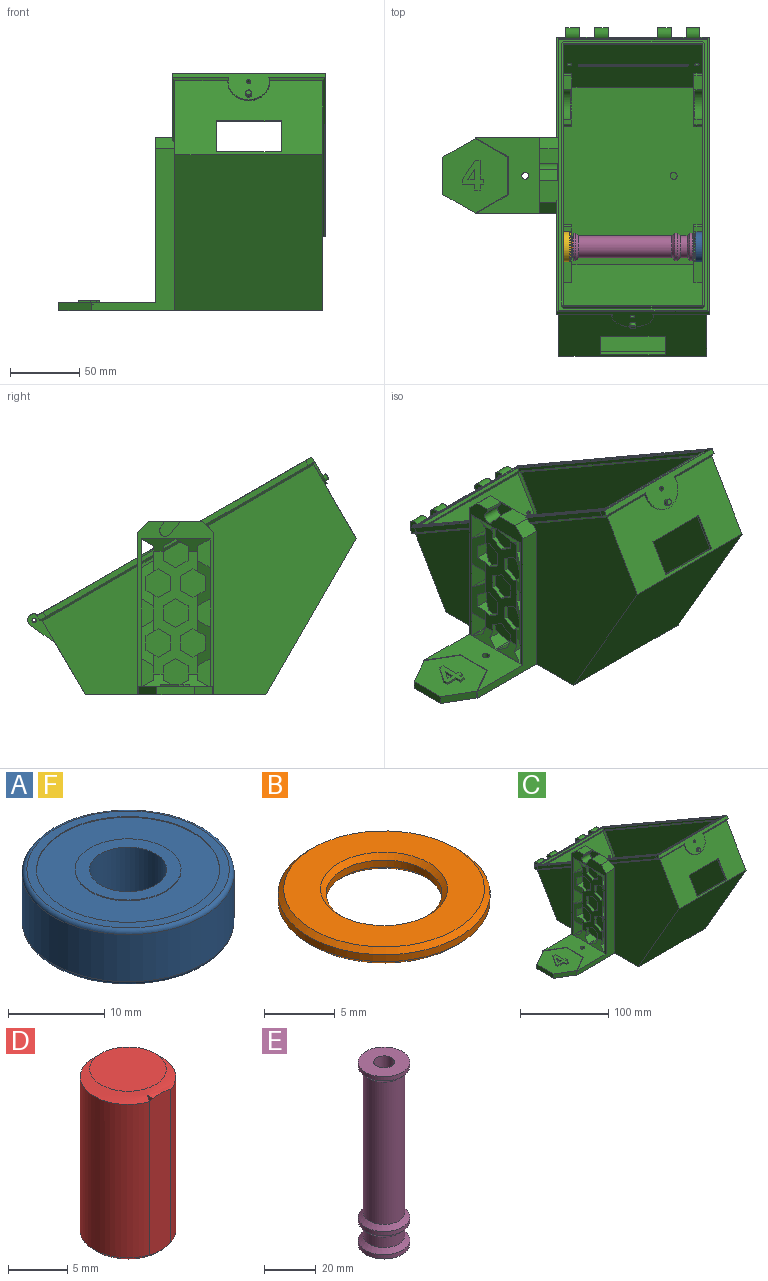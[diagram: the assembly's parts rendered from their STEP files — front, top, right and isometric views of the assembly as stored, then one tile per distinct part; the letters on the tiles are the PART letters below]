
ASSEMBLY  parts=6 mates=5
PART A: 14 faces, bbox 23.8x23.8x7 mm
  f0: cylinder r=5.5mm len=11mm, axis (0,0,-1), area 3.5mm2, adj f4,f6
  f1: cylinder r=4mm len=8mm, axis (0,0,-1), area 175.9mm2, adj f3,f4
  f2: cylinder r=5.5mm len=11mm, axis (0,0,-1), area 3.5mm2, adj f3,f5
  f3: plane 11x11mm, normal (0,0,1), area 44.8mm2, adj f1,f2
  f4: plane 11x11mm, normal (0,0,-1), area 44.8mm2, adj f0,f1
  f5: plane 19x19mm, normal (0,0,1), area 188.5mm2, adj f2,f8
  f6: plane 19x19mm, normal (0,0,-1), area 188.5mm2, adj f0,f7
  f7: cylinder r=9.5mm len=19mm, axis (0,0,-1), area 6mm2, adj f6,f11
  f8: cylinder r=9.5mm len=19mm, axis (0,0,-1), area 6mm2, adj f5,f10
  f9: cylinder r=11mm len=22mm, axis (0,0,-1), area 414.7mm2, adj f12,f13
  f10: plane 21x21mm, normal (0,0,1), area 62.8mm2, adj f8,f13
  f11: plane 21x21mm, normal (0,0,-1), area 62.8mm2, adj f7,f12
  f12: torus R=10.5mm, axis (0,0,1), area 53.4mm2, adj f9,f11
  f13: torus R=10.5mm, axis (0,0,1), area 53.4mm2, adj f9,f10
PART B: 8 faces, bbox 15x15x1.4 mm
  f0: cylinder r=4.1mm len=8.2mm, axis (0,0,-1), area 15.5mm2, adj f5,f7
  f1: cylinder r=7.5mm len=15mm, axis (0,0,-1), area 28.3mm2, adj f4,f6
  f2: plane 14.2x14.2mm, normal (0,0,1), area 94.8mm2, adj f4,f5
  f3: plane 14.2x14.2mm, normal (0,0,-1), area 94.8mm2, adj f6,f7
  f4: cone r=7.1mm half-angle=45deg, axis (0,0,-1), area 25.9mm2, adj f1,f2
  f5: cone r=4.1mm half-angle=45deg, axis (0,0,1), area 15.3mm2, adj f0,f2
  f6: cone r=7.5mm half-angle=45deg, axis (0,0,1), area 25.9mm2, adj f1,f3
  f7: cone r=4.5mm half-angle=45deg, axis (0,0,-1), area 15.3mm2, adj f0,f3
PART C: 307 faces, bbox 193.2x238.3x172.8 mm
  f0: cylinder r=2.5mm len=5mm, axis (0,0,-1), area 22mm2, adj f1,f55
  f1: plane 5x5mm, normal (0,0,1), area 19.6mm2, adj f0
  f2: cylinder r=1.6mm len=10mm, axis (-1,0,0), area 100.5mm2, adj f244,f253
  f3: cylinder r=1.6mm len=10mm, axis (-1,0,0), area 100.5mm2, adj f238,f240
  f4: plane 107.8x0.92mm, normal (0,1,-0.01), area 98.9mm2, adj f5,f26,f302,f303
  f5: plane 107.8x1.04mm, normal (0,0.87,-0.5), area 129.4mm2, adj f4,f302,f303,f306
  f6: plane 107.8x0.79mm, normal (0,-0.51,0.86), area 98.9mm2, adj f7,f26,f301,f302
  f7: plane 107.8x1.04mm, normal (0,-0.87,0.5), area 129.4mm2, adj f6,f301,f302,f306
  f8: plane 198.81x115.33mm, normal (-0.71,-0.35,-0.61), area 432.4mm2, adj f9,f10,f11,f12,f13,f251,f252,f257
  f9: plane 227.12x166.81mm, normal (-1,0,0), area 21083.7mm2, adj f8,f13,f227,f228,f229,f230,f285,f289
  f10: plane 70.94x40.96mm, normal (0,-0.5,-0.87), area 8.9mm2, adj f8,f13,f252,f253,f254,f255,f256,f284
  f11: plane 26.85x15.5mm, normal (0,-0.5,-0.87), area 3.1mm2, adj f8,f257,f282,f299
  f12: plane 78.58x45.37mm, normal (0,-0.5,-0.87), area 13.2mm2, adj f8,f247,f248,f249,f250,f251,f290,f305
  f13: plane 117.98x60.6mm, normal (0,1,0), area 1916.5mm2, adj f8,f9,f10,f26,f30,f283,f284,f285
  f14: cone r=2.1mm half-angle=45deg, axis (0,0.87,-0.5), area 5.6mm2, adj f15,f16
  f15: cylinder r=2.25mm len=5.25mm, axis (0,-0.87,0.5), area 38.2mm2, adj f14,f249
  f16: plane 3.9x3.38mm, normal (0,-0.87,0.5), area 11.9mm2, adj f14
  f17: plane 2.48x2.3mm, normal (-0.71,0.61,-0.35), area 4.2mm2, adj f18,f19,f25,f306
  f18: plane 100.55x1.73mm, normal (0,0.87,-0.5), area 201.1mm2, adj f17,f19,f20,f306
  f19: plane 192.23x110.99mm, normal (0,0.5,0.87), area 835.1mm2, adj f17,f18,f20,f21,f22,f23,f24,f25
  f20: plane 2.48x2.3mm, normal (0.71,0.61,-0.35), area 4.2mm2, adj f18,f19,f21,f306
  f21: plane 190.63x111.22mm, normal (1,0,0), area 437.9mm2, adj f19,f20,f22,f306
  f22: plane 2.48x2.3mm, normal (0.71,-0.61,0.35), area 4.2mm2, adj f19,f21,f23,f306
  f23: plane 100.55x1.73mm, normal (0,-0.87,0.5), area 201.1mm2, adj f19,f22,f24,f306
  f24: plane 2.48x2.3mm, normal (-0.71,-0.61,0.35), area 4.2mm2, adj f19,f23,f25,f306
  f25: plane 190.63x111.22mm, normal (-1,0,0), area 437.9mm2, adj f17,f19,f24,f306
  f26: plane 198.99x114.89mm, normal (0,0.5,0.87), area 678.3mm2, adj f4,f6,f13,f27,f30,f231,f232,f233
  f27: plane 39x13.71mm, normal (0,0,1), area 373.2mm2, adj f26,f30,f290,f293,f294,f295,f296,f297
  f28: plane 0.7x0.68mm, normal (0.85,-0.52,0), area 0.2mm2, adj f29,f30,f276,f298
  f29: plane 0.47x0.29mm, normal (0,0.5,0.87), area 0.1mm2, adj f28,f30,f276
  f30: plane 193.23x112.72mm, normal (1,0,0), area 870.7mm2, adj f13,f26,f27,f28,f29,f281,f297,f298
  f31: plane 7.34x4.94mm, normal (0,0,1), area 18.1mm2, adj f50,f51,f52
  f32: plane 17.29x7.95mm, normal (0,0,1), area 120.8mm2, adj f41,f42,f46,f53,f54,f72,f76
  f33: plane 17.29x7.95mm, normal (0,0,1), area 120.8mm2, adj f35,f36,f48,f56,f57,f73,f76
  f34: plane 22.1x13.04mm, normal (1,0,0), area 73.5mm2, adj f49,f59,f60,f61
  f35: plane 22.1x13.04mm, normal (1,0,0), area 73.5mm2, adj f33,f36,f48,f61
  f36: cylinder r=8.98mm len=17.96mm, axis (-1,0,0), area 24.2mm2, adj f33,f35,f56,f61
  f37: plane 7.85x1.5mm, normal (0,0.71,0.71), area 15.1mm2, adj f39,f40,f56,f61
  f38: plane 21.53x6.35mm, normal (0,1,0), area 136.7mm2, adj f43,f54,f55,f63
  f39: plane 21.53x6.35mm, normal (0,1,0), area 136.7mm2, adj f37,f55,f56,f65
  f40: plane 74.11x1.5mm, normal (-0.71,0,0.71), area 154mm2, adj f37,f61,f62,f65
  f41: cylinder r=8.98mm len=17.96mm, axis (-1,0,0), area 24.2mm2, adj f32,f42,f54,f66
  f42: plane 22.1x13.04mm, normal (-1,0,0), area 73.5mm2, adj f32,f41,f46,f66
  f43: plane 7.85x1.5mm, normal (0,0.71,0.71), area 15.1mm2, adj f38,f45,f54,f66
  f44: plane 22.1x13.04mm, normal (-1,0,0), area 73.5mm2, adj f47,f66,f67,f68
  f45: plane 74.11x1.5mm, normal (0.71,0,0.71), area 154mm2, adj f43,f63,f66,f70
  f46: cylinder r=11.05mm len=22.1mm, axis (-1,0,0), area 278.8mm2, adj f32,f42,f66,f72
  f47: cylinder r=11.05mm len=22.1mm, axis (1,0,0), area 278.8mm2, adj f44,f66,f68,f72
  f48: cylinder r=11.05mm len=22.1mm, axis (-1,0,0), area 278.8mm2, adj f33,f35,f61,f73
  f49: cylinder r=11.05mm len=22.1mm, axis (1,0,0), area 278.8mm2, adj f34,f59,f61,f73
  f50: plane 7.34x1.5mm, normal (-1,0,0), area 11mm2, adj f31,f51,f52,f74
  f51: plane 7.34x4.94mm, normal (0.83,-0.56,0), area 13.3mm2, adj f31,f50,f52,f74
  f52: plane 4.94x1.5mm, normal (0,1,0), area 7.4mm2, adj f31,f50,f51,f74
  f53: plane 88.26x52mm, normal (0.71,0.61,0.35), area 228.8mm2, adj f32,f72,f75,f76
  f54: plane 41.99x23.03mm, normal (1,0,0), area 650.7mm2, adj f32,f38,f41,f43,f55,f66,f76
  f55: plane 128.5x100.95mm, normal (0,0,1), area 12223.7mm2, adj f0,f38,f39,f54,f56,f63,f64,f65
  f56: plane 41.99x23.03mm, normal (-1,0,0), area 650.7mm2, adj f33,f36,f37,f39,f55,f61,f76
  f57: plane 88.26x52mm, normal (-0.71,0.61,0.35), area 228.8mm2, adj f33,f73,f76,f77
  f58: plane 6.35x3.4mm, normal (0,0.87,-0.5), area 24.9mm2, adj f59,f78,f79,f80
  f59: plane 17.29x7.95mm, normal (0,0,1), area 87.8mm2, adj f34,f49,f58,f60,f73,f78,f80,f91
  f60: cylinder r=8.98mm len=17.96mm, axis (1,0,0), area 24.2mm2, adj f34,f59,f61,f80
  f61: plane 85.49x7.95mm, normal (0,0,1), area 67.4mm2, adj f34,f35,f36,f37,f40,f48,f49,f56
  f62: plane 7.85x1.5mm, normal (0,-0.71,0.71), area 15.1mm2, adj f40,f61,f64,f80
  f63: plane 71.11x21.53mm, normal (1,0,0), area 1530.8mm2, adj f38,f45,f55,f69
  f64: plane 21.53x6.35mm, normal (0,-1,0), area 136.7mm2, adj f55,f62,f65,f80
  f65: plane 71.11x21.53mm, normal (-1,0,0), area 1530.8mm2, adj f39,f40,f55,f64
  f66: plane 85.49x7.95mm, normal (0,0,1), area 67.4mm2, adj f41,f42,f43,f44,f45,f46,f47,f54
  f67: cylinder r=8.98mm len=17.96mm, axis (1,0,0), area 24.2mm2, adj f44,f66,f68,f81
  f68: plane 17.29x7.95mm, normal (0,0,1), area 87.8mm2, adj f44,f47,f67,f71,f72,f81,f83,f86
  f69: plane 21.53x6.35mm, normal (0,-1,0), area 136.7mm2, adj f55,f63,f70,f81
  f70: plane 7.85x1.5mm, normal (0,-0.71,0.71), area 15.1mm2, adj f45,f66,f69,f81
  f71: plane 6.35x3.4mm, normal (0,0.87,-0.5), area 24.9mm2, adj f68,f81,f82,f83
  f72: plane 220.59x154.32mm, normal (1,0,0), area 17869.6mm2, adj f32,f46,f47,f53,f66,f68,f85,f86
  f73: plane 220.59x154.32mm, normal (-1,0,0), area 17869.6mm2, adj f33,f48,f49,f57,f59,f61,f89,f90
  f74: plane 21.56x15.44mm, normal (0,0,1), area 165.5mm2, adj f50,f51,f52,f92,f93,f94,f95,f96
  f75: plane 2.77x1.6mm, normal (0.55,0.84,0), area 2.6mm2, adj f53,f87,f103
  f76: plane 109.9x100.95mm, normal (0,0.87,0.5), area 12473mm2, adj f32,f33,f53,f54,f55,f56,f57,f103
  f77: plane 2.77x1.6mm, normal (-0.55,0.84,0), area 2.6mm2, adj f57,f89,f103
  f78: plane 7.16x5.65mm, normal (-1,0,0), area 23.5mm2, adj f58,f59,f79,f108
  f79: plane 6.35x3.9mm, normal (0,0.5,0.87), area 28.6mm2, adj f58,f78,f80,f108
  f80: plane 38.73x23.03mm, normal (-1,0,0), area 627.2mm2, adj f55,f58,f59,f60,f61,f62,f64,f79
  f81: plane 38.73x23.03mm, normal (1,0,0), area 627.2mm2, adj f55,f66,f67,f68,f69,f70,f71,f82
  f82: plane 6.35x3.9mm, normal (0,0.5,0.87), area 28.6mm2, adj f71,f81,f83,f108
  f83: plane 7.16x5.65mm, normal (1,0,0), area 23.5mm2, adj f68,f71,f82,f108
  f84: plane 101.15x0.09mm, normal (0,-0.5,-0.87), area 10.1mm2, adj f86,f91,f108,f111
  f85: plane 190.15x109.79mm, normal (0,-0.5,-0.87), area 21.9mm2, adj f72,f86,f87,f112
  f86: plane 31.8x19.63mm, normal (0.71,-0.61,0.35), area 82.2mm2, adj f68,f72,f84,f85,f108,f111,f112
  f87: plane 54.03x31.66mm, normal (0.71,0.61,-0.35), area 138.5mm2, adj f72,f75,f85,f88,f110,f112,f113
  f88: plane 101.15x0.09mm, normal (0,-0.5,-0.87), area 10.1mm2, adj f87,f89,f110,f113
  f89: plane 54.03x31.66mm, normal (-0.71,0.61,-0.35), area 138.5mm2, adj f73,f77,f88,f90,f110,f113,f114
  f90: plane 190.15x109.79mm, normal (0,-0.5,-0.87), area 21.9mm2, adj f73,f89,f91,f114
  f91: plane 31.8x19.63mm, normal (-0.71,-0.61,0.35), area 82.2mm2, adj f59,f73,f84,f90,f108,f111,f114
  f92: plane 3.98x1.5mm, normal (0,-1,0), area 6mm2, adj f74,f93,f102,f116
  f93: plane 4.32x1.5mm, normal (1,0,0), area 6.5mm2, adj f74,f92,f94,f116
  f94: plane 2.67x1.5mm, normal (0,-1,0), area 4mm2, adj f74,f93,f95,f116
  f95: plane 3.62x1.5mm, normal (1,0,0), area 5.4mm2, adj f74,f94,f96,f116
  f96: plane 2.67x1.5mm, normal (0,1,0), area 4mm2, adj f74,f95,f97,f116
  f97: plane 13.62x1.5mm, normal (1,0,0), area 20.4mm2, adj f74,f96,f98,f116
  f98: plane 3.46x1.5mm, normal (0,1,0), area 5.2mm2, adj f74,f97,f99,f116
  f99: plane 13.64x9.32mm, normal (-0.83,0.56,0), area 24.8mm2, adj f74,f98,f100,f116
  f100: plane 3.6x1.5mm, normal (-1,0,0), area 5.4mm2, adj f74,f99,f101,f116
  f101: plane 8.79x1.5mm, normal (0,-1,0), area 13.2mm2, adj f74,f100,f102,f116
  f102: plane 4.32x1.5mm, normal (-1,0,0), area 6.5mm2, adj f74,f92,f101,f116
  f103: plane 100.95x2.77mm, normal (0,1,0), area 249.2mm2, adj f75,f76,f77,f110,f117,f118,f119
  f104: cylinder r=1.75mm len=3.5mm, axis (0,1,0), area 5.6mm2, adj f105,f107,f108,f122
  f105: plane 76.2x1.11mm, normal (0,0,-1), area 84.5mm2, adj f104,f106,f108,f123
  f106: cylinder r=1.75mm len=3.5mm, axis (0,1,0), area 5.6mm2, adj f105,f107,f108,f124
  f107: plane 76.2x1.11mm, normal (0,0,1), area 84.5mm2, adj f104,f106,f108,f125
  f108: plane 101.37x54.25mm, normal (0,-0.87,0.5), area 5684.1mm2, adj f55,f78,f79,f80,f81,f82,f83,f84
  f109: plane 198.81x115.33mm, normal (0.71,-0.35,-0.61), area 483.8mm2, adj f121,f126,f136,f141
  f110: plane 100.95x52.44mm, normal (0,0.87,-0.5), area 4902.8mm2, adj f87,f88,f89,f103,f117,f119,f120,f147
  f111: plane 102.55x2.05mm, normal (0,-0.97,-0.26), area 215.9mm2, adj f84,f86,f91,f112,f114,f163
  f112: plane 191.37x111.03mm, normal (0.71,-0.35,-0.61), area 467.2mm2, adj f85,f86,f87,f111,f113,f164
  f113: plane 102.55x2.05mm, normal (0,0.26,-0.97), area 215.9mm2, adj f87,f88,f89,f112,f114,f165
  f114: plane 191.37x111.03mm, normal (-0.71,-0.35,-0.61), area 467.2mm2, adj f89,f90,f91,f111,f113,f166
  f115: plane 22.98x9mm, normal (-0.85,0,0.52), area 117mm2, adj f181,f183,f207,f216,f217,f218
  f116: plane 54.04x46.81mm, normal (0,0,1), area 1713.2mm2, adj f92,f93,f94,f95,f96,f97,f98,f99
  f117: plane 23.94x14.88mm, normal (1,0,0), area 52.7mm2, adj f103,f110,f118,f120,f227
  f118: plane 46.7x2.02mm, normal (0,0.5,0.87), area 108.7mm2, adj f103,f117,f119,f227
  f119: plane 23.94x14.88mm, normal (-1,0,0), area 52.7mm2, adj f103,f110,f118,f120,f227
  f120: plane 46.7x1.73mm, normal (0,-0.5,-0.87), area 93.4mm2, adj f110,f117,f119,f227
  f121: plane 40.6x2.06mm, normal (0,-0.97,-0.26), area 84.2mm2, adj f109,f141,f142,f227
  f122: bspline ~5.58x3.82mm, area 13mm2, adj f104,f123,f125,f230
  f123: plane 76.2x1.8mm, normal (0,0.5,-0.87), area 158.4mm2, adj f105,f122,f124,f230
  f124: bspline ~5.58x3.82mm, area 13mm2, adj f106,f123,f125,f230
  f125: plane 76.2x1.04mm, normal (0,0.87,0.5), area 91.4mm2, adj f107,f122,f124,f230
  f126: plane 227.12x166.81mm, normal (1,0,0), area 21412.8mm2, adj f109,f227,f228,f229,f230
  f127: cylinder r=1.6mm len=3.77mm, axis (0,-0.87,0.5), area 20.1mm2, adj f108,f230
  f128: cylinder r=1.6mm len=3.77mm, axis (0,-0.87,0.5), area 20.1mm2, adj f108,f230
  f129: plane 35.59x0.09mm, normal (0,-0.5,-0.87), area 3.6mm2, adj f130,f232,f233,f234
  f130: plane 35.59x2.05mm, normal (0,0.26,-0.97), area 75.5mm2, adj f129,f230,f232,f234
  f131: cylinder r=1.35mm len=10mm, axis (-1,0,0), area 84.8mm2, adj f234,f236
  f132: plane 18.02x12.76mm, normal (0,0.58,-0.82), area 220.8mm2, adj f230,f234,f235,f236
  f133: plane 10.8x0.09mm, normal (0,-0.5,-0.87), area 1.1mm2, adj f134,f236,f237,f238
  f134: plane 10.8x2.05mm, normal (0,0.26,-0.97), area 22.9mm2, adj f133,f230,f236,f238
  f135: plane 18.02x12.76mm, normal (0,0.58,-0.82), area 220.8mm2, adj f230,f238,f239,f240
  f136: plane 6.5x2.05mm, normal (0,0.26,-0.97), area 12.2mm2, adj f109,f141,f230,f240
  f137: cylinder r=1.35mm len=10mm, axis (-1,0,0), area 84.8mm2, adj f232,f246
  f138: plane 18.02x12.76mm, normal (0,0.58,-0.82), area 220.8mm2, adj f230,f231,f232,f246
  f139: plane 10.8x0.09mm, normal (0,-0.5,-0.87), area 1.1mm2, adj f140,f244,f245,f246
  f140: plane 10.8x2.05mm, normal (0,0.26,-0.97), area 22.9mm2, adj f139,f230,f244,f246
  f141: plane 198.99x114.89mm, normal (0,-0.5,-0.87), area 27.7mm2, adj f109,f121,f136,f142,f240,f241,f242,f249
  f142: cylinder r=15.01mm len=9.72mm, axis (0,-0.87,0.5), area 15.8mm2, adj f121,f141,f143,f227,f249
  f143: plane 1.92x1.72mm, normal (0.86,-0.25,-0.44), area 2mm2, adj f142,f144,f227,f249
  f144: cylinder r=15.01mm len=12.11mm, axis (0,-0.87,0.5), area 23.2mm2, adj f143,f145,f227,f249
  f145: plane 1.39x1.23mm, normal (-0.01,-0.5,-0.87), area 2mm2, adj f144,f146,f227,f249
  f146: cylinder r=15.01mm len=12.03mm, axis (0,-0.87,0.5), area 23.2mm2, adj f145,f148,f227,f249
  f147: cylinder r=1.6mm len=4.72mm, axis (0,0.87,-0.5), area 36.2mm2, adj f110,f249
  f148: plane 1.92x1.73mm, normal (-0.87,-0.25,-0.43), area 2mm2, adj f146,f227,f249,f250
  f149: plane 18.02x12.76mm, normal (0,0.58,-0.82), area 220.8mm2, adj f230,f243,f244,f253
  f150: plane 14x9mm, normal (0,-0.5,-0.87), area 88.3mm2, adj f151,f260,f265,f267
  f151: plane 10.39x8.36mm, normal (0,-1,0), area 42.9mm2, adj f150,f152,f187,f214,f260,f267
  f152: plane 22.98x9mm, normal (-0.85,0,0.52), area 117mm2, adj f151,f186,f207,f212,f213,f214,f267
  f153: plane 10.39x9.72mm, normal (0,1,0), area 101mm2, adj f188,f192,f260,f267
  f154: plane 10.39x9.72mm, normal (0,1,0), area 101mm2, adj f193,f197,f260,f267
  f155: plane 14x9mm, normal (0,-0.5,-0.87), area 88.3mm2, adj f156,f260,f266,f267
  f156: plane 10.39x3mm, normal (0,-1,0), area 31.2mm2, adj f155,f157,f260,f267
  f157: plane 14x9mm, normal (0,-0.5,0.87), area 88.3mm2, adj f156,f260,f266,f267
  f158: plane 14x9mm, normal (0,-0.5,0.87), area 88.3mm2, adj f160,f260,f267,f268
  f159: plane 14x9mm, normal (0,-0.5,-0.87), area 108.9mm2, adj f160,f258,f259,f268,f269,f270
  f160: plane 10.39x7.29mm, normal (0,-1,0), area 38.7mm2, adj f158,f159,f258,f260,f267,f270
  f161: plane 10.39x9.72mm, normal (0,-1,0), area 101mm2, adj f167,f171,f210,f272
  f162: plane 10.39x9.72mm, normal (0,-1,0), area 101mm2, adj f175,f179,f209,f274
  f163: plane 100.95x2.17mm, normal (0,-0.87,0.5), area 252.4mm2, adj f19,f111,f164,f166
  f164: plane 191.23x111.85mm, normal (1,0,0), area 548.4mm2, adj f19,f112,f163,f165
  f165: plane 100.95x2.17mm, normal (0,0.87,-0.5), area 252.4mm2, adj f19,f113,f164,f166
  f166: plane 191.23x111.85mm, normal (-1,0,0), area 548.4mm2, adj f19,f114,f163,f165
  f167: plane 9.72x9mm, normal (0,-0.5,-0.87), area 52.5mm2, adj f161,f168,f207,f210,f272,f278
  f168: plane 9x5.2mm, normal (0,0.5,-0.87), area 31.2mm2, adj f167,f169,f207,f278
  f169: plane 10.39x3mm, normal (0,1,0), area 31.2mm2, adj f168,f170,f207,f278
  f170: plane 9x5.2mm, normal (0,0.5,0.87), area 31.2mm2, adj f169,f171,f207,f278
  f171: plane 9.72x9mm, normal (0,-0.5,0.87), area 52.5mm2, adj f161,f170,f207,f210,f272,f278
  f172: plane 14x9mm, normal (0,0.5,-0.87), area 88.3mm2, adj f173,f207,f210,f272,f273,f278
  f173: plane 10.39x3mm, normal (0,1,0), area 31.2mm2, adj f172,f174,f207,f278
  f174: plane 14x9mm, normal (0,0.5,0.87), area 88.3mm2, adj f173,f207,f209,f273,f274,f278
  f175: plane 9.72x9mm, normal (0,-0.5,-0.87), area 52.5mm2, adj f162,f176,f207,f209,f274,f278
  f176: plane 9x5.2mm, normal (0,0.5,-0.87), area 31.2mm2, adj f175,f177,f207,f278
  f177: plane 10.39x3mm, normal (0,1,0), area 31.2mm2, adj f176,f178,f207,f278
  f178: plane 9x5.2mm, normal (0,0.5,0.87), area 31.2mm2, adj f177,f179,f207,f278
  f179: plane 9.72x9mm, normal (0,-0.5,0.87), area 52.5mm2, adj f162,f178,f207,f209,f274,f278
  f180: plane 14x9mm, normal (0,0.5,-0.87), area 88.3mm2, adj f181,f207,f209,f274,f275,f278
  f181: plane 10.39x8.36mm, normal (0,1,0), area 42.9mm2, adj f115,f180,f182,f207,f216,f278
  f182: plane 22.98x9mm, normal (0.85,0,0.52), area 117mm2, adj f181,f183,f215,f216,f218,f278
  f183: plane 10.39x8.36mm, normal (0,-1,0), area 42.9mm2, adj f115,f182,f184,f207,f218,f278
  f184: plane 9x5.2mm, normal (0,-0.5,-0.87), area 31.2mm2, adj f183,f185,f207,f278
  f185: plane 9x5.2mm, normal (0,0.5,-0.87), area 31.2mm2, adj f184,f186,f207,f278
  f186: plane 10.39x8.36mm, normal (0,1,0), area 42.9mm2, adj f152,f185,f187,f207,f212,f278
  f187: plane 22.98x9mm, normal (0.85,0,0.52), area 117mm2, adj f151,f186,f211,f212,f214,f260,f278
  f188: plane 9.72x9mm, normal (0,0.5,0.87), area 52.5mm2, adj f153,f189,f207,f260,f267,f278
  f189: plane 9x5.2mm, normal (0,-0.5,0.87), area 31.2mm2, adj f188,f190,f207,f278
  f190: plane 10.39x3mm, normal (0,-1,0), area 31.2mm2, adj f189,f191,f207,f278
  f191: plane 9x5.2mm, normal (0,-0.5,-0.87), area 31.2mm2, adj f190,f192,f207,f278
  f192: plane 9.72x9mm, normal (0,0.5,-0.87), area 52.5mm2, adj f153,f191,f207,f260,f267,f278
  f193: plane 9.72x9mm, normal (0,0.5,0.87), area 52.5mm2, adj f154,f194,f207,f260,f267,f278
  f194: plane 9x5.2mm, normal (0,-0.5,0.87), area 31.2mm2, adj f193,f195,f207,f278
  f195: plane 10.39x3mm, normal (0,-1,0), area 31.2mm2, adj f194,f196,f207,f278
  f196: plane 9x5.2mm, normal (0,-0.5,-0.87), area 31.2mm2, adj f195,f197,f207,f278
  f197: plane 9.72x9mm, normal (0,0.5,-0.87), area 52.5mm2, adj f154,f196,f207,f260,f267,f278
  f198: plane 10.39x7.29mm, normal (0,1,0), area 38.7mm2, adj f199,f207,f257,f258,f270,f278
  f199: plane 9x5.2mm, normal (0,0.5,0.87), area 31.2mm2, adj f198,f206,f207,f278
  f200: plane 9x5.2mm, normal (0,-0.5,0.87), area 31.2mm2, adj f201,f205,f207,f278
  f201: plane 10.39x3mm, normal (0,-1,0), area 31.2mm2, adj f200,f202,f207,f278
  f202: plane 9x5.2mm, normal (0,-0.5,-0.87), area 31.2mm2, adj f201,f203,f207,f278
  f203: plane 9x5.2mm, normal (0,0.5,-0.87), area 31.2mm2, adj f202,f204,f207,f278
  f204: plane 10.39x3mm, normal (0,1,0), area 31.2mm2, adj f203,f205,f207,f278
  f205: plane 9x5.2mm, normal (0,0.5,0.87), area 31.2mm2, adj f200,f204,f207,f278
  f206: plane 9x5.2mm, normal (0,-0.5,0.87), area 31.2mm2, adj f199,f207,f278,f279
  f207: plane 89.1x32mm, normal (-1,0,0), area 1421.1mm2, adj f115,f152,f167,f168,f169,f170,f171,f172
  f208: plane 14x9mm, normal (0,0.5,0.87), area 88.3mm2, adj f207,f210,f272,f277,f278,f299
  f209: plane 32.91x9mm, normal (0.85,-0.52,0), area 204.8mm2, adj f162,f174,f175,f179,f180,f278,f283
  f210: plane 32.91x9mm, normal (0.85,-0.52,0), area 204.8mm2, adj f161,f167,f171,f172,f208,f278,f283
  f211: plane 23.64x0.19mm, normal (1,0,0), area 4.4mm2, adj f187,f212,f214,f285
  f212: plane 14x8.32mm, normal (0,0.5,0.87), area 108.5mm2, adj f152,f186,f187,f211,f213,f285
  f213: plane 23.64x0.19mm, normal (-1,0,0), area 4.4mm2, adj f152,f212,f214,f285
  f214: plane 14x8.32mm, normal (0,-0.5,0.87), area 108.5mm2, adj f151,f152,f187,f211,f213,f285
  f215: plane 23.64x0.19mm, normal (1,0,0), area 4.4mm2, adj f182,f216,f218,f285
  f216: plane 14x8.32mm, normal (0,0.5,0.87), area 108.5mm2, adj f115,f181,f182,f215,f217,f285
  f217: plane 23.64x0.19mm, normal (-1,0,0), area 4.4mm2, adj f115,f216,f218,f285
  f218: plane 14x8.32mm, normal (0,-0.5,0.87), area 108.5mm2, adj f115,f182,f183,f215,f217,f285
  f219: plane 27.6x1.51mm, normal (-1,0,0), area 41.7mm2, adj f262,f285,f286,f287
  f220: plane 23.4x13.5mm, normal (0.5,-0.87,0), area 40.8mm2, adj f116,f221,f226,f287
  f221: plane 27.02x1.51mm, normal (1,0,0), area 40.8mm2, adj f116,f220,f222,f287
  f222: plane 23.4x13.52mm, normal (0.5,0.87,0), area 40.8mm2, adj f116,f221,f224,f287
  f223: cylinder r=2.5mm len=5.98mm, axis (0,0,-1), area 94mm2, adj f285,f289
  f224: plane 23.4x13.5mm, normal (-0.5,0.87,0), area 161.7mm2, adj f116,f222,f225,f288,f289
  f225: plane 27.02x5.98mm, normal (-1,0,0), area 161.7mm2, adj f116,f224,f226,f289
  f226: plane 23.4x13.52mm, normal (-0.5,-0.87,0), area 161.7mm2, adj f116,f220,f225,f261,f289
  f227: plane 107.19x53.53mm, normal (0,-0.87,0.5), area 4990.2mm2, adj f9,f117,f118,f119,f120,f121,f126,f142
  f228: plane 113.29x107.19mm, normal (0,-0.87,-0.5), area 14021.6mm2, adj f9,f126,f227,f229
  f229: plane 130.81x107.19mm, normal (0,0,-1), area 14021.6mm2, adj f9,f126,f228,f230
  f230: plane 107.19x53.53mm, normal (0,0.87,-0.5), area 5352.1mm2, adj f9,f122,f123,f124,f125,f126,f127,f128
  f231: cylinder r=4.65mm len=10mm, axis (-1,0,0), area 146.6mm2, adj f26,f138,f232,f246
  f232: plane 21.2x19.98mm, normal (1,0,0), area 132.6mm2, adj f26,f129,f130,f137,f138,f230,f231,f233
  f233: plane 35.59x3.46mm, normal (0,0.87,-0.5), area 142.4mm2, adj f26,f129,f232,f234
  f234: plane 21.2x19.98mm, normal (-1,0,0), area 132.6mm2, adj f26,f129,f130,f131,f132,f230,f233,f235
  f235: cylinder r=4.65mm len=10mm, axis (-1,0,0), area 146.6mm2, adj f26,f132,f234,f236
  f236: plane 21.2x19.98mm, normal (1,0,0), area 132.6mm2, adj f26,f131,f132,f133,f134,f230,f235,f237
  f237: plane 10.8x3.46mm, normal (0,0.87,-0.5), area 43.2mm2, adj f26,f133,f236,f238
  f238: plane 21.2x19.98mm, normal (-1,0,0), area 130.3mm2, adj f3,f26,f133,f134,f135,f230,f237,f239
  f239: cylinder r=4.65mm len=10mm, axis (-1,0,0), area 146.6mm2, adj f26,f135,f238,f240
  f240: plane 21.2x19.98mm, normal (1,0,0), area 130.3mm2, adj f3,f26,f135,f136,f141,f230,f239,f241
  f241: plane 6.6x3.46mm, normal (0,0.87,-0.5), area 26.4mm2, adj f26,f141,f240,f242
  f242: plane 200.99x118.35mm, normal (1,0,0), area 919.1mm2, adj f26,f141,f241,f249
  f243: cylinder r=4.65mm len=10mm, axis (-1,0,0), area 146.6mm2, adj f26,f149,f244,f253
  f244: plane 21.2x19.98mm, normal (1,0,0), area 130.3mm2, adj f2,f26,f139,f140,f149,f230,f243,f245
  f245: plane 10.8x3.46mm, normal (0,0.87,-0.5), area 43.2mm2, adj f26,f139,f244,f246
  f246: plane 21.2x19.98mm, normal (-1,0,0), area 132.6mm2, adj f26,f137,f138,f139,f140,f230,f231,f245
  f247: plane 3.46x2mm, normal (0,0.87,-0.5), area 0mm2, adj f12,f26,f248,f290
  f248: plane 6.5x6.06mm, normal (-1,0,0), area 20.8mm2, adj f12,f26,f247,f249
  f249: plane 110.4x19.28mm, normal (0,-0.87,0.5), area 868.6mm2, adj f12,f15,f26,f141,f142,f143,f144,f145
  f250: cylinder r=15.01mm len=9.59mm, axis (0,-0.87,0.5), area 15.6mm2, adj f12,f148,f227,f249,f251
  f251: plane 40.29x2.06mm, normal (0,-0.97,-0.26), area 83.6mm2, adj f8,f12,f227,f250
  f252: plane 6.5x2.05mm, normal (0,0.26,-0.97), area 12.2mm2, adj f8,f10,f230,f253
  f253: plane 21.2x19.98mm, normal (-1,0,0), area 130.3mm2, adj f2,f10,f26,f149,f230,f243,f252,f254
  f254: plane 6.61x3.46mm, normal (0,0.87,-0.5), area 26.4mm2, adj f10,f26,f253,f255
  f255: plane 6.5x6.06mm, normal (-1,0,0), area 20.8mm2, adj f10,f26,f254,f256
  f256: plane 3.46x2mm, normal (0,-0.87,0.5), area 0mm2, adj f10,f26,f255,f284
  f257: plane 12.82x9mm, normal (0,0.5,-0.87), area 106.3mm2, adj f8,f11,f198,f258,f270,f280,f282
  f258: plane 22.67x9mm, normal (0.85,0,-0.52), area 127.4mm2, adj f8,f159,f160,f198,f257,f259,f260,f278
  f259: plane 0.7x0.7mm, normal (0.85,0.52,0), area 0.1mm2, adj f159,f258,f291
  f260: plane 89.1x9mm, normal (0.85,0.52,0), area 409.7mm2, adj f150,f151,f153,f154,f155,f156,f157,f158
  f261: plane 4.47x0.48mm, normal (-1,0,0), area 2.1mm2, adj f226,f287,f289,f292
  f262: plane 23.74x13.69mm, normal (-0.5,0.87,0), area 41.4mm2, adj f219,f285,f287,f292
  f263: plane 13.2x2.57mm, normal (0,-0.77,-0.63), area 43.9mm2, adj f264,f294,f295,f296
  f264: cylinder r=4.1mm len=13.2mm, axis (1,0,0), area 170mm2, adj f263,f293,f294,f296
  f265: plane 20.39x14mm, normal (0,1,0), area 285.5mm2, adj f150,f285,f291,f296
  f266: plane 20.78x14mm, normal (0,1,0), area 291mm2, adj f155,f157,f291,f296
  f267: plane 89.1x9mm, normal (-0.85,0.52,0), area 409.7mm2, adj f150,f151,f152,f153,f154,f155,f156,f157
  f268: plane 20.78x14mm, normal (0,1,0), area 291mm2, adj f158,f159,f291,f296
  f269: plane 0.7x0.7mm, normal (-0.85,0.52,0), area 0.1mm2, adj f159,f270,f296
  f270: plane 50x9mm, normal (-0.85,0,-0.52), area 269.4mm2, adj f159,f160,f198,f207,f257,f267,f269,f271
  f271: plane 0.7x0.7mm, normal (-0.85,-0.52,0), area 0.1mm2, adj f270,f276,f296
  f272: plane 32.91x9mm, normal (-0.85,-0.52,0), area 204.8mm2, adj f161,f167,f171,f172,f207,f208,f296
  f273: plane 20.78x14mm, normal (0,-1,0), area 291mm2, adj f172,f174,f283,f296
  f274: plane 32.91x9mm, normal (-0.85,-0.52,0), area 204.8mm2, adj f162,f174,f175,f179,f180,f207,f296
  f275: plane 20.39x14mm, normal (0,-1,0), area 285.5mm2, adj f180,f283,f285,f296
  f276: plane 14x9mm, normal (0,0.5,-0.87), area 108.9mm2, adj f28,f29,f270,f271,f277,f298,f299
  f277: plane 10.39x7.29mm, normal (0,1,0), area 38.7mm2, adj f207,f208,f270,f276,f278,f298
  f278: plane 89.1x32mm, normal (1,0,0), area 1421.1mm2, adj f167,f168,f169,f170,f171,f172,f173,f174
  f279: plane 10.39x7.29mm, normal (0,-1,0), area 38.7mm2, adj f206,f207,f270,f278,f280,f298
  f280: plane 12.23x9mm, normal (0,-0.5,-0.87), area 105.5mm2, adj f257,f270,f279,f282,f298
  f281: plane 22.38x12.92mm, normal (0,0.5,0.87), area 30.8mm2, adj f30,f282,f298,f299
  f282: plane 26.85x16.56mm, normal (-1,0,0), area 81.7mm2, adj f11,f257,f280,f281,f298,f299
  f283: plane 88.71x2.5mm, normal (1,0,0), area 220mm2, adj f8,f13,f209,f210,f273,f275,f285,f299
  f284: plane 68.44x42.98mm, normal (-1,0,0), area 311.5mm2, adj f10,f13,f26,f256
  f285: plane 60.45x55mm, normal (0,0,1), area 1592.7mm2, adj f9,f13,f211,f212,f213,f214,f215,f216
  f286: plane 23.73x13.71mm, normal (-0.5,-0.87,0), area 41.4mm2, adj f13,f219,f285,f287
  f287: plane 55x23.91mm, normal (0,0,1), area 40.9mm2, adj f13,f219,f220,f221,f222,f261,f262,f286
  f288: plane 4.47x0.48mm, normal (-1,0,0), area 2.1mm2, adj f13,f224,f287,f289
  f289: plane 84.01x55mm, normal (0,0,-1), area 4262.3mm2, adj f9,f13,f223,f224,f225,f226,f261,f288
  f290: plane 77.82x46.23mm, normal (-1,0,0), area 344.6mm2, adj f12,f26,f27,f247,f305
  f291: plane 116.45x20.32mm, normal (1,0,0), area 371.8mm2, adj f8,f258,f259,f260,f265,f266,f268,f285
  f292: plane 117.98x60.62mm, normal (0,-1,0), area 1930.5mm2, adj f9,f261,f262,f285,f287,f289,f291,f296
  f293: plane 13.2x9.6mm, normal (0,0.77,0.63), area 163.9mm2, adj f27,f264,f294,f296
  f294: plane 15.14x11.1mm, normal (-1,0,0), area 102mm2, adj f27,f263,f264,f293,f295
  f295: plane 13.2x1.83mm, normal (0,-1,0), area 24.1mm2, adj f27,f263,f294,f296
  f296: plane 120x55mm, normal (-1,0,0), area 1069.7mm2, adj f13,f27,f263,f264,f265,f266,f267,f268
  f297: plane 13.71x8mm, normal (0,0.71,0.71), area 155.1mm2, adj f13,f27,f30,f296
  f298: plane 21.9x8.53mm, normal (0.85,0,-0.52), area 115.2mm2, adj f28,f30,f276,f277,f278,f279,f280,f281
  f299: plane 20.78x14mm, normal (0,-1,0), area 280.4mm2, adj f8,f11,f30,f208,f276,f281,f282,f283
  f300: plane 1.73x1mm, normal (0,0.87,-0.5), area 0mm2, adj f26,f30,f301,f306
  f301: plane 3.64x3.03mm, normal (1,0,0), area 5.4mm2, adj f6,f7,f26,f300,f306
  f302: plane 198.13x115.54mm, normal (-1,0,0), area 454.7mm2, adj f4,f5,f6,f7,f26,f306
  f303: plane 3.26x3.25mm, normal (1,0,0), area 5.4mm2, adj f4,f5,f26,f304,f306
  f304: plane 1.73x1mm, normal (0,-0.87,0.5), area 0mm2, adj f26,f30,f303,f306
  f305: plane 14x8mm, normal (0,-0.71,0.71), area 151.7mm2, adj f8,f12,f27,f290,f291,f292,f296
  f306: plane 196.74x113.59mm, normal (0,0.5,0.87), area 1506.2mm2, adj f5,f7,f17,f18,f20,f21,f22,f23
PART D: 6 faces, bbox 8.1x8.1x17 mm
  f0: cylinder r=4.03mm len=15.8mm, axis (0,0,-1), area 359.3mm2, adj f1,f4,f5
  f1: plane 16.21x2.51mm, normal (0,-1,0), area 40.3mm2, adj f0,f4,f5
  f2: plane 6.45x6.45mm, normal (0,0,1), area 32.7mm2, adj f4
  f3: plane 7.25x7.25mm, normal (0,0,-1), area 41.3mm2, adj f5
  f4: cone r=3.23mm half-angle=45deg, axis (0,0,-1), area 25.3mm2, adj f0,f1,f2
  f5: cone r=4.03mm half-angle=45deg, axis (0,0,1), area 13.1mm2, adj f0,f1,f3
PART E: 15 faces, bbox 20x20x86.6 mm
  f0: cylinder r=10mm len=20mm, axis (0,0,-1), area 125.7mm2, adj f1,f10
  f1: plane 20x20mm, normal (0,0,-1), area 263.9mm2, adj f0,f11
  f2: cylinder r=8mm len=16mm, axis (0,0,-1), area 251.3mm2, adj f9,f10
  f3: cylinder r=10mm len=20mm, axis (0,0,-1), area 125.7mm2, adj f7,f9
  f4: cylinder r=8mm len=67.6mm, axis (0,0,-1), area 3397.9mm2, adj f7,f8
  f5: cylinder r=10mm len=20mm, axis (0,0,-1), area 125.7mm2, adj f6,f8
  f6: plane 20x20mm, normal (0,0,1), area 263.9mm2, adj f5,f14
  f7: cone r=8mm half-angle=45deg, axis (0,0,-1), area 159.9mm2, adj f3,f4
  f8: cone r=10mm half-angle=45deg, axis (0,0,1), area 159.9mm2, adj f4,f5
  f9: cone r=10mm half-angle=45deg, axis (0,0,1), area 159.9mm2, adj f2,f3
  f10: cone r=8mm half-angle=45deg, axis (0,0,-1), area 159.9mm2, adj f0,f2
  f11: cylinder r=4mm len=8.6mm, axis (0,0,-1), area 216.1mm2, adj f1,f12
  f12: cone r=0mm half-angle=59deg, axis (0,0,-1), area 58.6mm2, adj f11
  f13: cone r=0mm half-angle=59deg, axis (0,0,1), area 58.6mm2, adj f14
  f14: cylinder r=4mm len=8.6mm, axis (0,0,1), area 216.1mm2, adj f6,f13
PART F: same geometry as A
PLACE A rot(axis=(0.71,0,0.71),180deg) t=(544.98,-24,22.04)mm
PLACE B rot(axis=(0.71,0,0.71),180deg) t=(451.68,-24,22.04)mm
PLACE C at identity fixed
PLACE D rot(axis=(-0.58,0.58,-0.58),120deg) t=(445.48,-24,22.04)mm
PLACE E rot(axis=(0,-1,0),90deg) t=(541.68,-24,22.04)mm
PLACE F rot(axis=(0.71,0,-0.71),180deg) t=(447.83,-24,22.04)mm
MATE revolute A.f9 <-> C.f36  axis (1,0,0) through (548.48,-24,22.04)mm
MATE revolute E.f0 <-> A.f1  axis (1,0,0) through (539.68,-24,22.04)mm
MATE revolute B.f0 <-> E.f13  axis (1,0,0) through (453.08,-24,22.04)mm
MATE revolute F.f9 <-> C.f36  axis (-1,0,0) through (444.33,-24,22.04)mm
MATE revolute D.f0 <-> E.f13  axis (1,0,0) through (461.68,-24,22.04)mm
